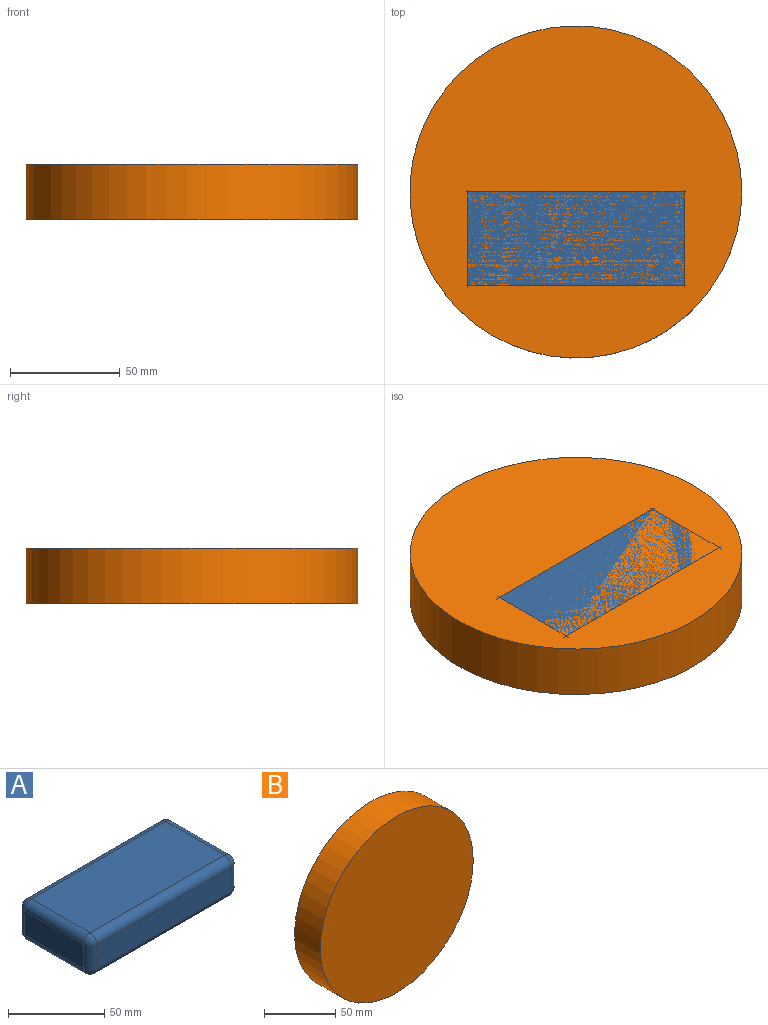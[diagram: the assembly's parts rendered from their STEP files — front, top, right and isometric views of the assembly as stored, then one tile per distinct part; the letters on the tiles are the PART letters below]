
ASSEMBLY  parts=2 mates=1
PART A: 26 faces, bbox 108.9x53x25.4 mm
  f0: plane 42.87x15.24mm, normal (-1,0,0), area 653.3mm2, adj f16,f20,f22,f25
  f1: plane 98.69x15.24mm, normal (0,-1,0), area 1504mm2, adj f6,f7,f21,f25
  f2: plane 42.87x15.24mm, normal (1,0,0), area 653.3mm2, adj f7,f9,f10,f14
  f3: plane 98.69x15.24mm, normal (0,1,0), area 1504mm2, adj f10,f13,f15,f16
  f4: plane 98.69x42.87mm, normal (0,0,1), area 4230.9mm2, adj f6,f9,f13,f20
  f5: plane 98.69x42.87mm, normal (0,0,-1), area 4230.9mm2, adj f14,f15,f21,f22
  f6: cylinder r=5.08mm len=98.69mm, axis (-1,0,0), area 787.5mm2, adj f1,f4,f8,f23
  f7: cylinder r=5.08mm len=15.24mm, axis (0,0,1), area 121.6mm2, adj f1,f2,f8,f18
  f8: sphere r=5.08mm, area 40.5mm2, adj f6,f7,f9
  f9: cylinder r=5.08mm len=42.87mm, axis (0,-1,0), area 342.1mm2, adj f2,f4,f8,f11
  f10: cylinder r=5.08mm len=15.24mm, axis (0,0,-1), area 121.6mm2, adj f2,f3,f11,f12
  f11: sphere r=5.08mm, area 40.5mm2, adj f9,f10,f13
  f12: sphere r=5.08mm, area 40.5mm2, adj f10,f14,f15
  f13: cylinder r=5.08mm len=98.69mm, axis (1,0,0), area 787.5mm2, adj f3,f4,f11,f17
  f14: cylinder r=5.08mm len=42.87mm, axis (0,1,0), area 342.1mm2, adj f2,f5,f12,f18
  f15: cylinder r=5.08mm len=98.69mm, axis (-1,0,0), area 787.5mm2, adj f3,f5,f12,f19
  f16: cylinder r=5.08mm len=15.24mm, axis (0,0,1), area 121.6mm2, adj f0,f3,f17,f19
  f17: sphere r=5.08mm, area 40.5mm2, adj f13,f16,f20
  f18: sphere r=5.08mm, area 40.5mm2, adj f7,f14,f21
  f19: sphere r=5.08mm, area 40.5mm2, adj f15,f16,f22
  f20: cylinder r=5.08mm len=42.87mm, axis (0,1,0), area 342.1mm2, adj f0,f4,f17,f23
  f21: cylinder r=5.08mm len=98.69mm, axis (1,0,0), area 787.5mm2, adj f1,f5,f18,f24
  f22: cylinder r=5.08mm len=42.87mm, axis (0,-1,0), area 342.1mm2, adj f0,f5,f19,f24
  f23: sphere r=5.08mm, area 40.5mm2, adj f6,f20,f25
  f24: sphere r=5.08mm, area 40.5mm2, adj f21,f22,f25
  f25: cylinder r=5.08mm len=15.24mm, axis (0,0,-1), area 121.6mm2, adj f0,f1,f23,f24
PART B: 3 faces, bbox 151.4x25.4x151.4 mm
  f0: cylinder r=75.72mm len=151.45mm, axis (0,1,0), area 12084.8mm2, adj f1,f2
  f1: plane 151.45x151.45mm, normal (0,-1,0), area 18013.5mm2, adj f0
  f2: plane 151.45x151.45mm, normal (0,1,0), area 18013.5mm2, adj f0
PLACE A t=(-42.15,9.76,38.45)mm
PLACE B rot(axis=(-1,0,0),90deg) t=(-42.15,31.2,38.45)mm
MATE fastened B.f0 <-> A.f5  axis (0,0,-1) through (-42.15,31.2,38.45)mm
